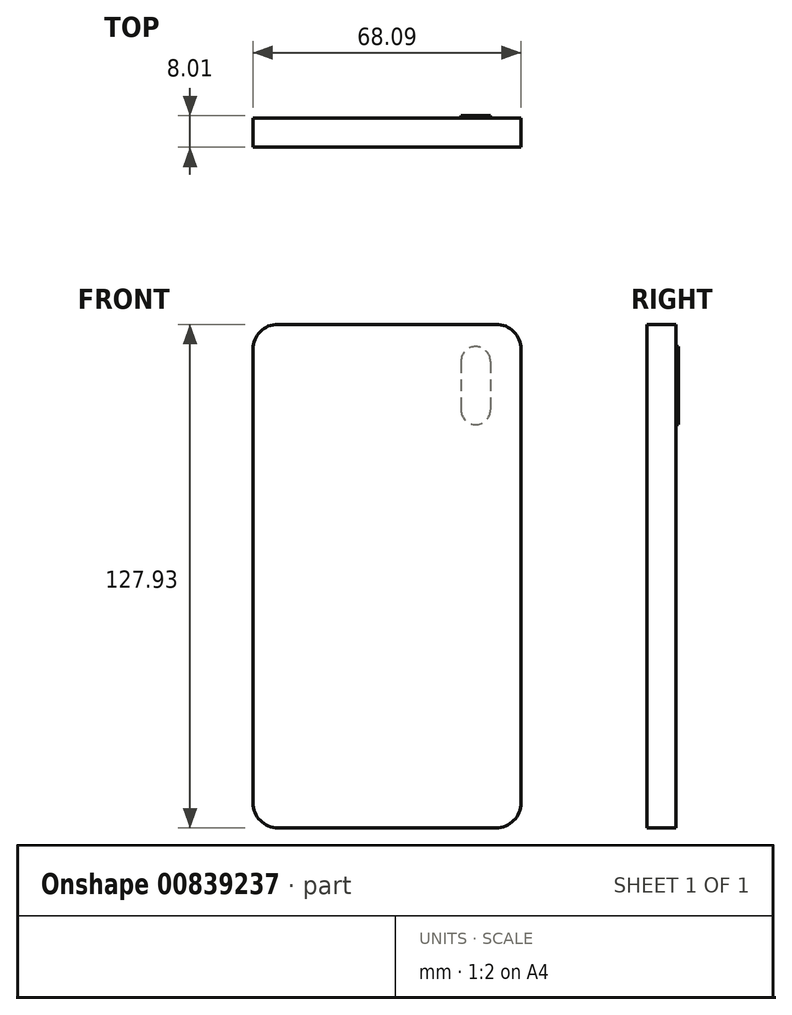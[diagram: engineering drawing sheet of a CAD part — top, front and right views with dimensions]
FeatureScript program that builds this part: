
annotation { "Feature Type Name" : "Feature", "Feature Type Description" : "" }
export const myFeature = defineFeature(function(context is Context, id is Id, definition is map)
    precondition{}
    {
        {
            var Q0;
            Q0=qCreatedBy(makeId("Front.planeOp"),FACE);
            var sketch = newSketch(context, id + "F0", { "sketchPlane" : qUnion([Q0])});
            skLineSegment(sketch, "E0.bottom", {"start": v(-36, 59.5) * mm, "end": v(19.38, 59.5) * mm});
            skLineSegment(sketch, "E0.top", {"start": v(-36, -68.43) * mm, "end": v(19.38, -68.43) * mm});
            skLineSegment(sketch, "E0.left", {"start": v(-42.36, 53.15) * mm, "end": v(-42.36, -62.08) * mm});
            skLineSegment(sketch, "E0.right", {"start": v(25.73, 53.15) * mm, "end": v(25.73, -62.08) * mm});
            skPoint(sketch, "E1.visualSharp", {"position": v(-42.36, 59.5) * mm});
            skArc(sketch, "E1.filletArc", {"start": v(-36, 59.5) * mm, "mid": v(-40.5, 57.64) * mm, "end": v(-42.36, 53.15) * mm});
            skPoint(sketch, "E2.visualSharp", {"position": v(25.73, 59.5) * mm});
            skArc(sketch, "E2.filletArc", {"start": v(25.73, 53.15) * mm, "mid": v(23.87, 57.64) * mm, "end": v(19.38, 59.5) * mm});
            skPoint(sketch, "E3.visualSharp", {"position": v(-42.36, -68.43) * mm});
            skArc(sketch, "E3.filletArc", {"start": v(-42.36, -62.08) * mm, "mid": v(-40.5, -66.57) * mm, "end": v(-36, -68.43) * mm});
            skPoint(sketch, "E4.visualSharp", {"position": v(25.73, -68.43) * mm});
            skArc(sketch, "E4.filletArc", {"start": v(19.38, -68.43) * mm, "mid": v(23.87, -66.57) * mm, "end": v(25.73, -62.08) * mm});
            skSolve(sketch);
        }
        {
            var Q0;
            Q0=makeQuery(id+"F0.imprint","IMPRINT",FACE,{"disambiguationData":[TD([[makeQuery(id+"F0.imprint","IMPRINT",EDGE,{"derivedFrom":sQuery(id+"F0.wireOp",EDGE,"E0.bottom")}),-1.0]])]});
            var sketch = newSketch(context, id + "F1", { "sketchPlane" : qUnion([Q0])});
            skSolve(sketch);
        }
        {
            var Q0;
            Q0=makeQuery(id+"F1.imprint","IMPRINT",FACE,{"disambiguationData":[TD([[makeQuery(id+"F1.imprint","IMPRINT",EDGE,{"derivedFrom":makeQuery(id+"F0.imprint","IMPRINT",EDGE,{"derivedFrom":sQuery(id+"F0.wireOp",EDGE,"E0.bottom")})}),-1.0]])]});
            extrude(context, id + "F2", {"entities" : qUnion([Q0]), "depth" : 7.37 * mm, "offsetDistance" : 25.4 * mm});
        }
        {
            var Q0;
            Q0=makeQuery(id+"F2.opExtrude","CAP_FACE",FACE,{"disambiguationData":[OSD([sQuery(id+"F0.wireOp",EDGE,"E0.bottom"),sQuery(id+"F0.wireOp",EDGE,"E0.top"),sQuery(id+"F0.wireOp",EDGE,"E0.left"),sQuery(id+"F0.wireOp",EDGE,"E0.right"),sQuery(id+"F0.wireOp",EDGE,"E1.filletArc"),sQuery(id+"F0.wireOp",EDGE,"E2.filletArc"),sQuery(id+"F0.wireOp",EDGE,"E3.filletArc"),sQuery(id+"F0.wireOp",EDGE,"E4.filletArc")])],"isStart":true});
            var sketch = newSketch(context, id + "F3", { "sketchPlane" : qUnion([Q0])});
            skLineSegment(sketch, "E5.bottom", {"start": v(-17.97, 50.1) * mm, "end": v(-10.5, 50.1) * mm});
            skLineSegment(sketch, "E5.top", {"start": v(-17.97, 37.73) * mm, "end": v(-10.5, 37.73) * mm});
            skLineSegment(sketch, "E5.left", {"start": v(-17.97, 50.1) * mm, "end": v(-17.97, 37.73) * mm});
            skLineSegment(sketch, "E5.right", {"start": v(-10.5, 50.1) * mm, "end": v(-10.5, 37.73) * mm});
            skSolve(sketch);
        }
        {
            var Q0;
            Q0=makeQuery(id+"F3.imprint","IMPRINT",FACE,{"disambiguationData":[TD([[makeQuery(id+"F3.imprint","IMPRINT",EDGE,{"derivedFrom":sQuery(id+"F3.wireOp",EDGE,"E5.bottom")}),-1.0]])]});
            extrude(context, id + "F4", {"entities" : qUnion([Q0]), "operationType" : NewBodyOperationType.ADD, "depth" : 0.64 * mm, "offsetDistance" : 25.4 * mm});
        }
        {
            var Q0;
            Q0=makeQuery(id+"F2.opExtrude","CAP_FACE",FACE,{"disambiguationData":[OSD([sQuery(id+"F0.wireOp",EDGE,"E0.bottom"),sQuery(id+"F0.wireOp",EDGE,"E0.top"),sQuery(id+"F0.wireOp",EDGE,"E0.left"),sQuery(id+"F0.wireOp",EDGE,"E0.right"),sQuery(id+"F0.wireOp",EDGE,"E1.filletArc"),sQuery(id+"F0.wireOp",EDGE,"E2.filletArc"),sQuery(id+"F0.wireOp",EDGE,"E3.filletArc"),sQuery(id+"F0.wireOp",EDGE,"E4.filletArc")])],"isStart":true});
            var sketch = newSketch(context, id + "F5", { "sketchPlane" : qUnion([Q0])});
            skArc(sketch, "E6", {"start": v(-10.5, 50.1) * mm, "mid": v(-14.24, 53.83) * mm, "end": v(-17.97, 50.1) * mm});
            skArc(sketch, "E7", {"start": v(-17.97, 37.73) * mm, "mid": v(-14.24, 34) * mm, "end": v(-10.5, 37.73) * mm});
            skSolve(sketch);
        }
        {
            var Q0;
            Q0=makeQuery(id+"F5.imprint","IMPRINT",FACE,{"disambiguationData":[TD([[makeQuery(id+"F5.imprint","IMPRINT",EDGE,{"derivedFrom":sQuery(id+"F5.wireOp",EDGE,"E7")}),1.0]])]});
            var Q1;
            Q1=makeQuery(id+"F5.imprint","IMPRINT",FACE,{"disambiguationData":[TD([[makeQuery(id+"F5.imprint","IMPRINT",EDGE,{"derivedFrom":sQuery(id+"F5.wireOp",EDGE,"E6")}),1.0]])]});
            extrude(context, id + "F6", {"entities" : qUnion([Q0, Q1]), "operationType" : NewBodyOperationType.ADD, "depth" : 0.64 * mm, "offsetDistance" : 25.4 * mm});
        }
        {
            var Q0;
            Q0=makeQuery(id+"F2.opExtrude","CAP_FACE",FACE,{"disambiguationData":[OSD([sQuery(id+"F0.wireOp",EDGE,"E0.bottom"),sQuery(id+"F0.wireOp",EDGE,"E0.top"),sQuery(id+"F0.wireOp",EDGE,"E0.left"),sQuery(id+"F0.wireOp",EDGE,"E0.right"),sQuery(id+"F0.wireOp",EDGE,"E1.filletArc"),sQuery(id+"F0.wireOp",EDGE,"E2.filletArc"),sQuery(id+"F0.wireOp",EDGE,"E3.filletArc"),sQuery(id+"F0.wireOp",EDGE,"E4.filletArc")])],"isStart":true});
            var sketch = newSketch(context, id + "F7", { "sketchPlane" : qUnion([Q0])});
            skCircle(sketch, "E8", {"center": v(-6.31, 47.3) * mm, "radius": 1.32 * mm});
            skSolve(sketch);
        }
        {
            var Q0;
            Q0=makeQuery(id+"F7.imprint","IMPRINT",FACE,{"disambiguationData":[TD([[makeQuery(id+"F7.imprint","IMPRINT",EDGE,{"derivedFrom":sQuery(id+"F7.wireOp",EDGE,"E8")}),1.0]])]});
            var Q1;
            Q1=makeQuery(id+"F7.imprint","IMPRINT",FACE,{"disambiguationData":[TD([[makeQuery(id+"F7.imprint","IMPRINT",EDGE,{"derivedFrom":sQuery(id+"F7.wireOp",EDGE,"E8")}),-1.0]])]});
            extrude(context, id + "F8", {"entities" : qUnion([Q0, Q1]), "operationType" : NewBodyOperationType.ADD, "oppositeDirection" : true, "depth" : 1.27 * mm, "offsetDistance" : 25.4 * mm});
        }
    });
